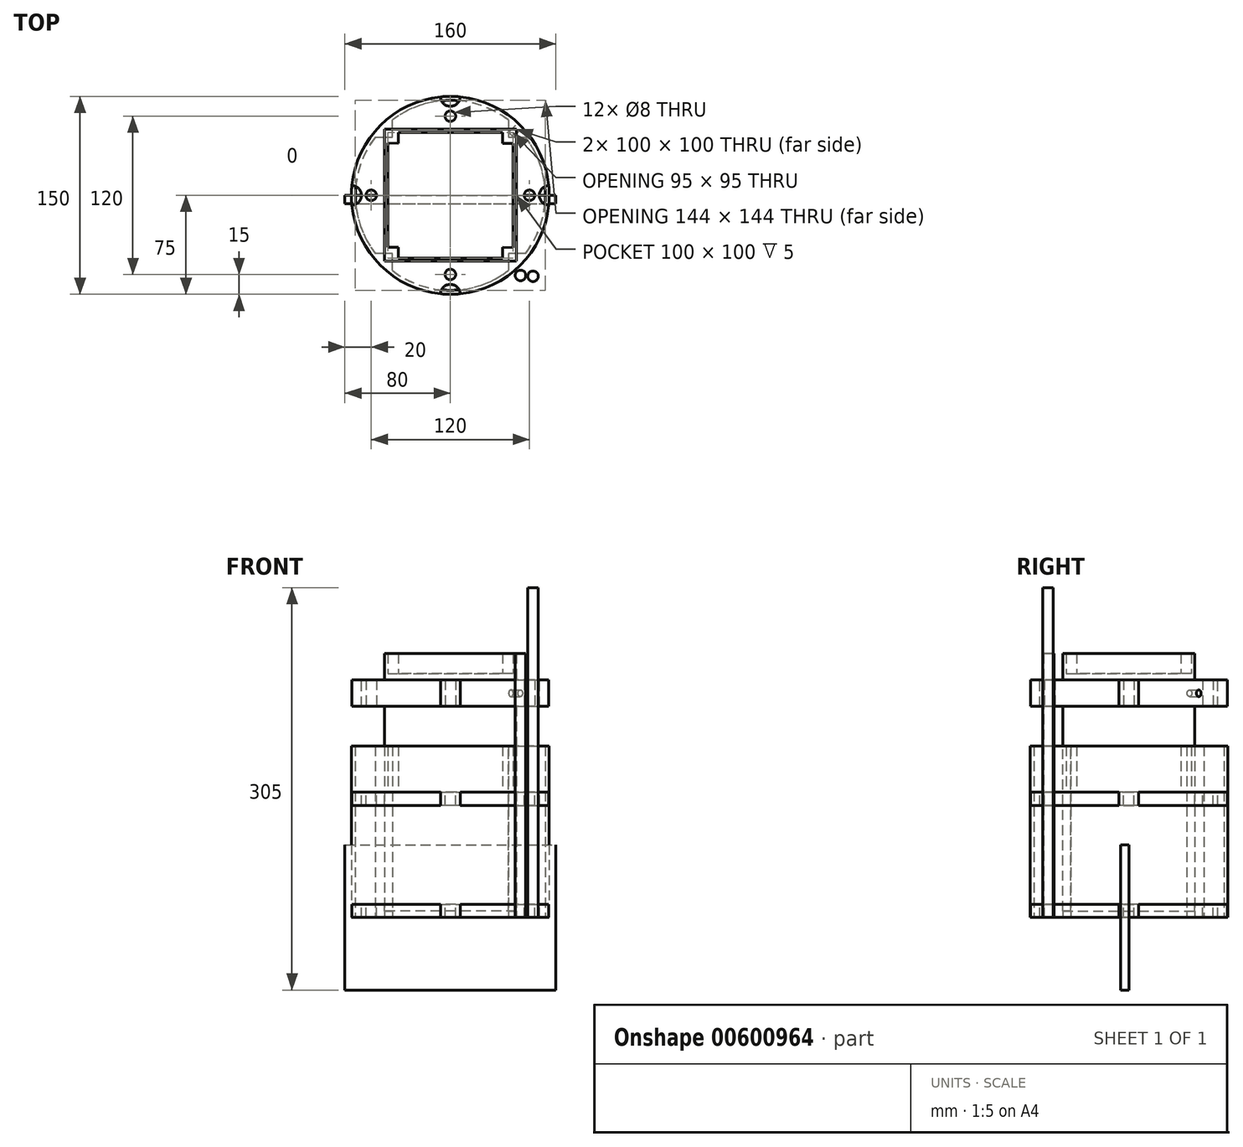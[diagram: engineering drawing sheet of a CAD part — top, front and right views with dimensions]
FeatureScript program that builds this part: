
annotation { "Feature Type Name" : "Feature", "Feature Type Description" : "" }
export const myFeature = defineFeature(function(context is Context, id is Id, definition is map)
    precondition{}
    {
        {
            var Q0;
            Q0=qCreatedBy(makeId("Top.planeOp"),FACE);
            var sketch = newSketch(context, id + "F0", { "sketchPlane" : qUnion([Q0])});
            skCircle(sketch, "E0", {"center": v(0, 0) * mm, "radius": 75 * mm});
            skSolve(sketch);
        }
        {
            var Q0;
            Q0=makeQuery(id+"F0.imprint","IMPRINT",FACE,{"disambiguationData":[TD([[makeQuery(id+"F0.imprint","IMPRINT",EDGE,{"derivedFrom":sQuery(id+"F0.wireOp",EDGE,"E0")}),1.0]])]});
            extrude(context, id + "F1", {"entities" : qUnion([Q0]), "depth" : 10 * mm, "offsetDistance" : 25 * mm});
        }
        {
            var Q0;
            Q0=makeQuery(id+"F1.opExtrude","CAP_FACE",FACE,{"disambiguationData":[OSD([sQuery(id+"F0.wireOp",EDGE,"E0")])],"isStart":false});
            var sketch = newSketch(context, id + "F2", { "sketchPlane" : qUnion([Q0])});
            skCircle(sketch, "E1", {"center": v(0, 60) * mm, "radius": 4 * mm});
            skCircle(sketch, "E2.1.0", {"center": v(-60, 0) * mm, "radius": 4 * mm});
            skCircle(sketch, "E2.2.0", {"center": v(0, -60) * mm, "radius": 4 * mm});
            skCircle(sketch, "E2.3.0", {"center": v(60, 0) * mm, "radius": 4 * mm});
            skPoint(sketch, "E2.center", {"position": v(0, 0) * mm});
            skSolve(sketch);
        }
        {
            var Q0;
            Q0 = qSketchRegion(id + "F2", true);
            extrude(context, id + "F3", {"entities" : qUnion([Q0]), "operationType" : NewBodyOperationType.REMOVE, "oppositeDirection" : true, "depth" : 25 * mm, "offsetDistance" : 25 * mm});
        }
        {
            var Q0;
            Q0=makeQuery(id+"F1.opExtrude","SWEPT_BODY",BODY,{"disambiguationData":[OSD([sQuery(id+"F0.wireOp",EDGE,"E0")])]});
            transform(context, id + "F4", {"entities" : qUnion([Q0]), "transformType" : TransformType.TRANSLATION_3D, "dx" : 0 * mm, "dy" : 0 * mm, "dz" : 85 * mm, "makeCopy" : true});
        }
        {
            var Q0;
            Q0=makeQuery(id+"F1.opExtrude","SWEPT_BODY",BODY,{"disambiguationData":[OSD([sQuery(id+"F0.wireOp",EDGE,"E0")])]});
            var Q1;
            Q1=makeQuery(id+"F4.opPattern","COPY",FACE,{"derivedFrom":makeQuery(id+"F1.opExtrude","CAP_FACE",FACE,{"disambiguationData":[OSD([sQuery(id+"F0.wireOp",EDGE,"E0")])],"isStart":true}),"instanceName":"1"});
            mirror(context, id + "F5", {"entities" : qUnion([Q0]), "mirrorPlane" : qUnion([Q1])});
        }
        {
            var Q0;
            Q0=qCreatedBy(makeId("Top.planeOp"),FACE);
            var sketch = newSketch(context, id + "F6", { "sketchPlane" : qUnion([Q0])});
            skCircle(sketch, "E3", {"center": v(62.63, -61.35) * mm, "radius": 4 * mm});
            skSolve(sketch);
        }
        {
            var Q0;
            Q0 = qSketchRegion(id + "F6", true);
            extrude(context, id + "F7", {"entities" : qUnion([Q0]), "depth" : 250 * mm, "offsetDistance" : 25 * mm});
        }
        {
            var Q0;
            Q0=makeQuery(id+"F5.opPattern","COPY",FACE,{"derivedFrom":makeQuery(id+"F1.opExtrude","CAP_FACE",FACE,{"disambiguationData":[OSD([sQuery(id+"F0.wireOp",EDGE,"E0")])],"isStart":true}),"instanceName":"1"});
            extrude(context, id + "F8", {"entities" : qUnion([Q0]), "operationType" : NewBodyOperationType.ADD, "depth" : 10 * mm, "offsetDistance" : 25 * mm});
        }
        {
            var Q0;
            Q0=qCreatedBy(makeId("Top.planeOp"),FACE);
            var sketch = newSketch(context, id + "F9", { "sketchPlane" : qUnion([Q0])});
            skLineSegment(sketch, "E4.bottom", {"start": v(50, 50) * mm, "end": v(-50, 50) * mm});
            skLineSegment(sketch, "E4.top", {"start": v(50, -50) * mm, "end": v(-50, -50) * mm});
            skLineSegment(sketch, "E4.left", {"start": v(50, 50) * mm, "end": v(50, -50) * mm});
            skLineSegment(sketch, "E4.right", {"start": v(-50, 50) * mm, "end": v(-50, -50) * mm});
            skPoint(sketch, "E4.middle", {"position": v(0, 0) * mm});
            skSolve(sketch);
        }
        {
            var Q0;
            Q0 = qSketchRegion(id + "F9", true);
            extrude(context, id + "F10", {"entities" : qUnion([Q0]), "depth" : 200 * mm, "offsetDistance" : 25 * mm});
        }
        {
            var Q0;
            Q0=makeQuery(id+"F8.opExtrude","CAP_FACE",FACE,{"disambiguationData":[OSD([sQuery(id+"F0.wireOp",EDGE,"E0")])],"isStart":false});
            var sketch = newSketch(context, id + "F11", { "sketchPlane" : qUnion([Q0])});
            skCircle(sketch, "E5", {"center": v(75, 0) * mm, "radius": 7.5 * mm});
            skCircle(sketch, "E6.1.0", {"center": v(0, 75) * mm, "radius": 7.5 * mm});
            skCircle(sketch, "E6.2.0", {"center": v(-75, 0) * mm, "radius": 7.5 * mm});
            skCircle(sketch, "E6.3.0", {"center": v(0, -75) * mm, "radius": 7.5 * mm});
            skPoint(sketch, "E6.center", {"position": v(0, 0) * mm});
            skSolve(sketch);
        }
        {
            var Q0;
            Q0 = qSketchRegion(id + "F11", true);
            extrude(context, id + "F12", {"entities" : qUnion([Q0]), "operationType" : NewBodyOperationType.REMOVE, "endBound" : BoundingType.THROUGH_ALL, "oppositeDirection" : true, "depth" : 25 * mm, "offsetDistance" : 25 * mm});
        }
        {
            var Q0;
            Q0=qCreatedBy(makeId("Right.planeOp"),FACE);
            var Q1;
            {var subQ0=sQuery(id+"F0.wireOp",EDGE,"E0");Q1=makeQuery(id+"F12.boolean.opBoolean","SPLIT",EDGE,{"disambiguationData":[TD([makeQuery(id+"F5.opPattern","COPY",FACE,{"derivedFrom":makeQuery(id+"F1.opExtrude","SWEPT_FACE",FACE,{"disambiguationData":[OSD([subQ0])]}),"instanceName":"1"}),makeQuery(id+"F8.opExtrude","SWEPT_FACE",FACE,{"disambiguationData":[OSD([subQ0])]}),makeQuery(id+"F8.opExtrude","CAP_FACE",FACE,{"disambiguationData":[OSD([subQ0])],"isStart":false}),makeQuery(id+"F12.opExtrude","SWEPT_FACE",FACE,{"disambiguationData":[OSD([sQuery(id+"F11.wireOp",EDGE,"E6.2.0")])]}),makeQuery(id+"F12.opExtrude","SWEPT_FACE",FACE,{"disambiguationData":[OSD([sQuery(id+"F11.wireOp",EDGE,"E6.3.0")])]})])],"derivedFrom":makeQuery(id+"F8.opExtrude","CAP_EDGE",EDGE,{"disambiguationData":[OSD([subQ0])],"isStart":false})});}
            cPlane(context, id + "F13", {"entities" : qUnion([Q0, Q1]), "cplaneType" : CPlaneType.LINE_ANGLE, "offset" : 25 * mm, "angle" : 45 * degree, "width" : 150 * mm, "height" : 150 * mm});
        }
        {
            var Q0;
            Q0=qCreatedBy(id+"F13.planeOp",FACE);
            cPlane(context, id + "F14", {"entities" : qUnion([Q0]), "cplaneType" : CPlaneType.OFFSET, "offset" : 75 * mm, "oppositeDirection" : true, "width" : 150 * mm, "height" : 150 * mm});
        }
        {
            var Q0;
            Q0=qCreatedBy(id+"F14.planeOp",FACE);
            var sketch = newSketch(context, id + "F15", { "sketchPlane" : qUnion([Q0])});
            skCircle(sketch, "E7", {"center": v(0, 170) * mm, "radius": 2.5 * mm});
            skSolve(sketch);
        }
        {
            var Q0;
            Q0 = qSketchRegion(id + "F15", true);
            extrude(context, id + "F16", {"entities" : qUnion([Q0]), "operationType" : NewBodyOperationType.REMOVE, "depth" : 10 * mm, "offsetDistance" : 25 * mm});
        }
        {
            var Q0;
            Q0=qCreatedBy(makeId("Top.planeOp"),FACE);
            var sketch = newSketch(context, id + "F17", { "sketchPlane" : qUnion([Q0])});
            skCircle(sketch, "E8", {"center": v(0, 0) * mm, "radius": 75 * mm});
            skArc(sketch, "E9", {"start": v(-57, 44) * mm, "mid": v(-72, 0) * mm, "end": v(-57, -44) * mm});
            skLineSegment(sketch, "E10", {"start": v(-57, 44) * mm, "end": v(-44, 44) * mm});
            skLineSegment(sketch, "E11", {"start": v(-44, 44) * mm, "end": v(-44, 57) * mm});
            skLineSegment(sketch, "E12.1.0", {"start": v(-44, -44) * mm, "end": v(-57, -44) * mm});
            skLineSegment(sketch, "E12.1.1", {"start": v(-44, -57) * mm, "end": v(-44, -44) * mm});
            skLineSegment(sketch, "E12.2.0", {"start": v(44, -44) * mm, "end": v(44, -57) * mm});
            skLineSegment(sketch, "E12.2.1", {"start": v(57, -44) * mm, "end": v(44, -44) * mm});
            skLineSegment(sketch, "E12.3.0", {"start": v(44, 44) * mm, "end": v(57, 44) * mm});
            skLineSegment(sketch, "E12.3.1", {"start": v(44, 57) * mm, "end": v(44, 44) * mm});
            skArc(sketch, "E13.trimOffspring", {"start": v(44, 57) * mm, "mid": v(0, 72) * mm, "end": v(-44, 57) * mm});
            skArc(sketch, "E14.trimOffspring", {"start": v(-44, -57) * mm, "mid": v(0, -72) * mm, "end": v(44, -57) * mm});
            skArc(sketch, "E15.trimOffspring", {"start": v(57, -44) * mm, "mid": v(72, 0) * mm, "end": v(57, 44) * mm});
            skSolve(sketch);
        }
        {
            var Q0;
            Q0 = qSketchRegion(id + "F17", true);
            extrude(context, id + "F18", {"entities" : qUnion([Q0]), "depth" : 130 * mm, "offsetDistance" : 25 * mm});
        }
        {
            var Q0;
            Q0=makeQuery(id+"F18.opExtrude","CAP_FACE",FACE,{"disambiguationData":[OSD([sQuery(id+"F17.wireOp",EDGE,"E8"),sQuery(id+"F17.wireOp",EDGE,"E9"),sQuery(id+"F17.wireOp",EDGE,"E10"),sQuery(id+"F17.wireOp",EDGE,"E11"),sQuery(id+"F17.wireOp",EDGE,"E12.1.0"),sQuery(id+"F17.wireOp",EDGE,"E12.1.1"),sQuery(id+"F17.wireOp",EDGE,"E12.2.0"),sQuery(id+"F17.wireOp",EDGE,"E12.2.1"),sQuery(id+"F17.wireOp",EDGE,"E12.3.0"),sQuery(id+"F17.wireOp",EDGE,"E12.3.1"),sQuery(id+"F17.wireOp",EDGE,"E13.trimOffspring"),sQuery(id+"F17.wireOp",EDGE,"E14.trimOffspring"),sQuery(id+"F17.wireOp",EDGE,"E15.trimOffspring")])],"isStart":false});
            var sketch = newSketch(context, id + "F19", { "sketchPlane" : qUnion([Q0])});
            skLineSegment(sketch, "E16.bottom", {"start": v(50, -50) * mm, "end": v(-50, -50) * mm});
            skLineSegment(sketch, "E16.top", {"start": v(50, 50) * mm, "end": v(-50, 50) * mm});
            skLineSegment(sketch, "E16.left", {"start": v(50, -50) * mm, "end": v(50, 50) * mm});
            skLineSegment(sketch, "E16.right", {"start": v(-50, -50) * mm, "end": v(-50, 50) * mm});
            skPoint(sketch, "E16.middle", {"position": v(0, 0) * mm});
            skSolve(sketch);
        }
        {
            var Q0;
            Q0 = qSketchRegion(id + "F19", true);
            extrude(context, id + "F20", {"entities" : qUnion([Q0]), "operationType" : NewBodyOperationType.REMOVE, "oppositeDirection" : true, "depth" : 125 * mm, "offsetDistance" : 25 * mm});
        }
        {
            var Q0;
            Q0=makeQuery(id+"F4.opPattern","COPY",FACE,{"derivedFrom":makeQuery(id+"F1.opExtrude","CAP_FACE",FACE,{"disambiguationData":[OSD([sQuery(id+"F0.wireOp",EDGE,"E0")])],"isStart":false}),"instanceName":"1"});
            var sketch = newSketch(context, id + "F21", { "sketchPlane" : qUnion([Q0])});
            skPoint(sketch, "E17.middle", {"position": v(0, 0) * mm});
            skLineSegment(sketch, "E18", {"start": v(39.5, -39.5) * mm, "end": v(39.5, -47.5) * mm});
            skLineSegment(sketch, "E19", {"start": v(39.5, -47.5) * mm, "end": v(-39.59, -47.5) * mm});
            skLineSegment(sketch, "E20", {"start": v(-39.59, -47.5) * mm, "end": v(-39.5, -39.5) * mm});
            skLineSegment(sketch, "E21.1.0", {"start": v(39.5, 39.5) * mm, "end": v(47.5, 39.5) * mm});
            skLineSegment(sketch, "E21.1.1", {"start": v(47.5, 39.5) * mm, "end": v(47.5, -39.59) * mm});
            skLineSegment(sketch, "E21.1.2", {"start": v(47.5, -39.59) * mm, "end": v(39.5, -39.5) * mm});
            skLineSegment(sketch, "E21.2.0", {"start": v(-39.5, 39.5) * mm, "end": v(-39.5, 47.5) * mm});
            skLineSegment(sketch, "E21.2.1", {"start": v(-39.5, 47.5) * mm, "end": v(39.59, 47.5) * mm});
            skLineSegment(sketch, "E21.2.2", {"start": v(39.59, 47.5) * mm, "end": v(39.5, 39.5) * mm});
            skLineSegment(sketch, "E21.3.0", {"start": v(-39.5, -39.5) * mm, "end": v(-47.5, -39.5) * mm});
            skLineSegment(sketch, "E21.3.1", {"start": v(-47.5, -39.5) * mm, "end": v(-47.5, 39.59) * mm});
            skLineSegment(sketch, "E21.3.2", {"start": v(-47.5, 39.59) * mm, "end": v(-39.5, 39.5) * mm});
            skSolve(sketch);
        }
        {
            var Q0;
            Q0 = qSketchRegion(id + "F21", true);
            extrude(context, id + "F22", {"entities" : qUnion([Q0]), "operationType" : NewBodyOperationType.ADD, "depth" : 12.8 * mm, "offsetDistance" : 25 * mm});
        }
        {
            var Q0;
            Q0=makeQuery(id+"F22.opExtrude","CAP_FACE",FACE,{"disambiguationData":[OSD([sQuery(id+"F21.wireOp",EDGE,"E18"),sQuery(id+"F21.wireOp",EDGE,"E19"),sQuery(id+"F21.wireOp",EDGE,"E20"),sQuery(id+"F21.wireOp",EDGE,"E21.1.0"),sQuery(id+"F21.wireOp",EDGE,"E21.1.1"),sQuery(id+"F21.wireOp",EDGE,"E21.1.2"),sQuery(id+"F21.wireOp",EDGE,"E21.2.0"),sQuery(id+"F21.wireOp",EDGE,"E21.2.1"),sQuery(id+"F21.wireOp",EDGE,"E21.2.2"),sQuery(id+"F21.wireOp",EDGE,"E21.3.0"),sQuery(id+"F21.wireOp",EDGE,"E21.3.1"),sQuery(id+"F21.wireOp",EDGE,"E21.3.2")])],"isStart":false});
            var sketch = newSketch(context, id + "F23", { "sketchPlane" : qUnion([Q0])});
            skCircle(sketch, "E22", {"center": v(-23.5, 44.25) * mm, "radius": 1.5 * mm});
            skCircle(sketch, "E23.MirrorC", {"center": v(23.5, 44.25) * mm, "radius": 1.5 * mm});
            skCircle(sketch, "E24.MirrorC", {"center": v(23.5, -44.25) * mm, "radius": 1.5 * mm});
            skCircle(sketch, "E25.MirrorC", {"center": v(-23.5, -44.25) * mm, "radius": 1.5 * mm});
            skSolve(sketch);
        }
        {
            var Q0;
            Q0 = qSketchRegion(id + "F23", true);
            extrude(context, id + "F24", {"entities" : qUnion([Q0]), "operationType" : NewBodyOperationType.REMOVE, "oppositeDirection" : true, "depth" : 25 * mm, "offsetDistance" : 25 * mm});
        }
        {
            var Q0;
            Q0=qCreatedBy(makeId("Front.planeOp"),FACE);
            var sketch = newSketch(context, id + "F25", { "sketchPlane" : qUnion([Q0])});
            skLineSegment(sketch, "E26.bottom", {"start": v(-80, 55) * mm, "end": v(80, 55) * mm});
            skLineSegment(sketch, "E26.top", {"start": v(-80, -55) * mm, "end": v(80, -55) * mm});
            skLineSegment(sketch, "E26.left", {"start": v(-80, 55) * mm, "end": v(-80, -55) * mm});
            skLineSegment(sketch, "E26.right", {"start": v(80, 55) * mm, "end": v(80, -55) * mm});
            skPoint(sketch, "E26.middle", {"position": v(0, 0) * mm});
            skSolve(sketch);
        }
        {
            var Q0;
            Q0=makeQuery(id+"F25.imprint","IMPRINT",FACE,{"disambiguationData":[TD([[makeQuery(id+"F25.imprint","IMPRINT",EDGE,{"derivedFrom":sQuery(id+"F25.wireOp",EDGE,"E26.bottom")}),-1.0]])]});
            extrude(context, id + "F26", {"entities" : qUnion([Q0]), "depth" : 6.2 * mm, "offsetDistance" : 25 * mm});
        }
        {
            var Q0;
            Q0 = qSketchRegion(id + "F21", true);
            extrude(context, id + "F27", {"entities" : qUnion([Q0]), "operationType" : NewBodyOperationType.REMOVE, "depth" : 150 * mm, "offsetDistance" : 25 * mm});
        }
        {
            var Q0;
            Q0 = qSketchRegion(id + "F21", true);
            extrude(context, id + "F28", {"entities" : qUnion([Q0]), "operationType" : NewBodyOperationType.ADD, "depth" : 90 * mm, "offsetDistance" : 25 * mm});
        }
        {
            var Q0;
            Q0=qCreatedBy(makeId("Top.planeOp"),FACE);
            var sketch = newSketch(context, id + "F29", { "sketchPlane" : qUnion([Q0])});
            skCircle(sketch, "E27", {"center": v(53.2, -60.72) * mm, "radius": 4 * mm});
            skSolve(sketch);
        }
        {
            var Q0;
            Q0=makeQuery(id+"F29.imprint","IMPRINT",FACE,{"disambiguationData":[TD([[makeQuery(id+"F29.imprint","IMPRINT",EDGE,{"derivedFrom":sQuery(id+"F29.wireOp",EDGE,"E27")}),1.0]])]});
            extrude(context, id + "F30", {"entities" : qUnion([Q0]), "depth" : 200 * mm, "offsetDistance" : 25 * mm});
        }
    });
